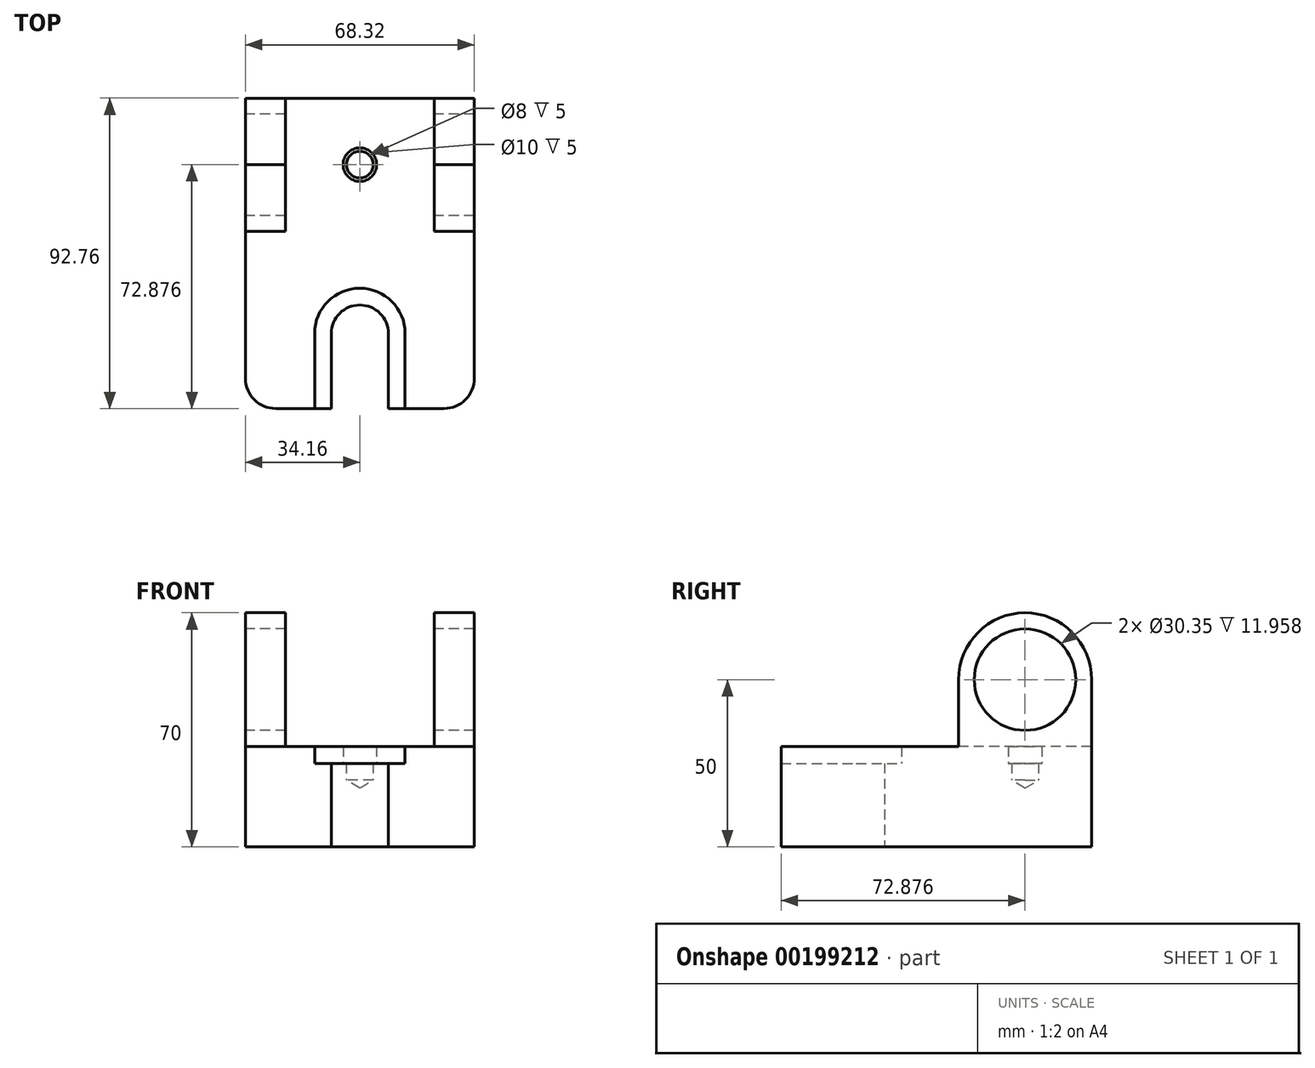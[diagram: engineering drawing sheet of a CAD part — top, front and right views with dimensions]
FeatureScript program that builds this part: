
annotation { "Feature Type Name" : "Feature", "Feature Type Description" : "" }
export const myFeature = defineFeature(function(context is Context, id is Id, definition is map)
    precondition{}
    {
        {
            var Q0;
            Q0=qCreatedBy(makeId("Top.planeOp"),FACE);
            var sketch = newSketch(context, id + "F0", { "sketchPlane" : qUnion([Q0])});
            skLineSegment(sketch, "E0.bottom", {"start": v(34.16, 46.38) * mm, "end": v(-34.16, 46.38) * mm});
            skLineSegment(sketch, "E0.top", {"start": v(34.16, -46.38) * mm, "end": v(13.5, -46.38) * mm});
            skLineSegment(sketch, "E0.left", {"start": v(34.16, 46.38) * mm, "end": v(34.16, -46.38) * mm});
            skLineSegment(sketch, "E0.right", {"start": v(-34.16, 46.38) * mm, "end": v(-34.16, -46.38) * mm});
            skPoint(sketch, "E0.middle", {"position": v(0, 0) * mm});
            skLineSegment(sketch, "E1", {"start": v(-13.5, -46.38) * mm, "end": v(-13.5, -23.93) * mm});
            skLineSegment(sketch, "E2", {"start": v(0, 46.38) * mm, "end": v(0, -46.38) * mm, "construction": true});
            skLineSegment(sketch, "E3.MirrorCS", {"start": v(13.5, -46.38) * mm, "end": v(13.5, -23.93) * mm});
            skArc(sketch, "E4", {"start": v(13.5, -23.93) * mm, "mid": v(0, -10.43) * mm, "end": v(-13.5, -23.93) * mm});
            skLineSegment(sketch, "E5.trimOffspring", {"start": v(-13.5, -46.38) * mm, "end": v(-34.16, -46.38) * mm});
            skLineSegment(sketch, "E6.0", {"start": v(8.5, -46.38) * mm, "end": v(8.5, -23.93) * mm});
            skArc(sketch, "E6.1", {"start": v(8.5, -23.93) * mm, "mid": v(0, -15.43) * mm, "end": v(-8.5, -23.93) * mm});
            skLineSegment(sketch, "E6.2", {"start": v(-8.5, -46.38) * mm, "end": v(-8.5, -23.93) * mm});
            skLineSegment(sketch, "E7", {"start": v(-13.5, -46.38) * mm, "end": v(-8.5, -46.38) * mm});
            skLineSegment(sketch, "E8", {"start": v(8.5, -46.38) * mm, "end": v(13.5, -46.38) * mm});
            skSolve(sketch);
        }
        {
            var Q0;
            Q0=makeQuery(id+"F0.imprint","IMPRINT",FACE,{"disambiguationData":[TD([[makeQuery(id+"F0.imprint","IMPRINT",EDGE,{"derivedFrom":sQuery(id+"F0.wireOp",EDGE,"E1")}),-1.0]])]});
            extrude(context, id + "F1", {"entities" : qUnion([Q0]), "depth" : 25 * mm});
        }
        {
            var Q0;
            Q0=makeQuery(id+"F0.imprint","IMPRINT",FACE,{"disambiguationData":[TD([[makeQuery(id+"F0.imprint","IMPRINT",EDGE,{"derivedFrom":sQuery(id+"F0.wireOp",EDGE,"E0.bottom")}),1.0]])]});
            extrude(context, id + "F2", {"entities" : qUnion([Q0]), "operationType" : NewBodyOperationType.ADD, "depth" : 30 * mm});
        }
        {
            var Q0;
            Q0=makeQuery(id+"F2.opExtrude","CAP_FACE",FACE,{"disambiguationData":[OSD([sQuery(id+"F0.wireOp",EDGE,"E0.bottom"),sQuery(id+"F0.wireOp",EDGE,"E0.top"),sQuery(id+"F0.wireOp",EDGE,"E0.left"),sQuery(id+"F0.wireOp",EDGE,"E0.right"),sQuery(id+"F0.wireOp",EDGE,"E1"),sQuery(id+"F0.wireOp",EDGE,"E3.MirrorCS"),sQuery(id+"F0.wireOp",EDGE,"E4"),sQuery(id+"F0.wireOp",EDGE,"E5.trimOffspring")])],"isStart":false});
            var sketch = newSketch(context, id + "F3", { "sketchPlane" : qUnion([Q0])});
            skLineSegment(sketch, "E9.bottom", {"start": v(34.16, 46.38) * mm, "end": v(22.2, 46.38) * mm});
            skLineSegment(sketch, "E9.top", {"start": v(34.16, 6.62) * mm, "end": v(22.2, 6.62) * mm});
            skLineSegment(sketch, "E9.left", {"start": v(34.16, 46.38) * mm, "end": v(34.16, 6.62) * mm});
            skLineSegment(sketch, "E9.right", {"start": v(22.2, 46.38) * mm, "end": v(22.2, 6.62) * mm});
            skLineSegment(sketch, "E10.MirrorCS", {"start": v(-22.2, 46.38) * mm, "end": v(-22.2, 6.62) * mm});
            skLineSegment(sketch, "E11.MirrorCS", {"start": v(-34.16, 6.62) * mm, "end": v(-22.2, 6.62) * mm});
            skLineSegment(sketch, "E12.MirrorCS", {"start": v(-34.16, 46.38) * mm, "end": v(-34.16, 6.62) * mm});
            skLineSegment(sketch, "E13.MirrorCS", {"start": v(-34.16, 46.38) * mm, "end": v(-22.2, 46.38) * mm});
            skSolve(sketch);
        }
        {
            var Q0;
            Q0=makeQuery(id+"F3.imprint","IMPRINT",FACE,{"disambiguationData":[TD([[makeQuery(id+"F3.imprint","IMPRINT",EDGE,{"derivedFrom":sQuery(id+"F3.wireOp",EDGE,"E9.bottom")}),1.0]])]});
            var Q1;
            Q1=makeQuery(id+"F3.imprint","IMPRINT",FACE,{"disambiguationData":[TD([[makeQuery(id+"F3.imprint","IMPRINT",EDGE,{"derivedFrom":sQuery(id+"F3.wireOp",EDGE,"E10.MirrorCS")}),-1.0]])]});
            extrude(context, id + "F4", {"entities" : qUnion([Q0, Q1]), "operationType" : NewBodyOperationType.ADD, "depth" : 40 * mm});
        }
        {
            var Q0;
            Q0=makeQuery(id+"F4.boolean.opBoolean","MERGE",FACE,{"derivedFrom":[makeQuery(id+"F2.opExtrude","SWEPT_FACE",FACE,{"disambiguationData":[OSD([sQuery(id+"F0.wireOp",EDGE,"E0.right")])]}),makeQuery(id+"F4.opExtrude","SWEPT_FACE",FACE,{"disambiguationData":[OSD([sQuery(id+"F3.wireOp",EDGE,"E12.MirrorCS")])]})]});
            var sketch = newSketch(context, id + "F5", { "sketchPlane" : qUnion([Q0])});
            skPoint(sketch, "E14", {"position": v(-26.5, 50) * mm});
            skPoint(sketch, "E14.positionSnap0", {"position": v(-6.62, 50) * mm});
            skPoint(sketch, "E14.positionSnap1", {"position": v(-26.5, 70) * mm});
            skCircle(sketch, "E15", {"center": v(-26.5, 50) * mm, "radius": 15.17 * mm});
            skSolve(sketch);
        }
        {
            var Q0;
            Q0=makeQuery(id+"F5.imprint","IMPRINT",FACE,{"disambiguationData":[TD([[makeQuery(id+"F5.imprint","IMPRINT",EDGE,{"derivedFrom":sQuery(id+"F5.wireOp",EDGE,"E15")}),1.0]])]});
            extrude(context, id + "F6", {"entities" : qUnion([Q0]), "operationType" : NewBodyOperationType.REMOVE, "endBound" : BoundingType.THROUGH_ALL, "oppositeDirection" : true, "depth" : 25 * mm});
        }
        {
            var Q0;
            Q0=makeQuery(id+"F4.opExtrude","CAP_EDGE",EDGE,{"disambiguationData":[OSD([sQuery(id+"F3.wireOp",EDGE,"E11.MirrorCS")])],"isStart":false});
            var Q1;
            Q1=makeQuery(id+"F4.opExtrude","CAP_EDGE",EDGE,{"disambiguationData":[OSD([sQuery(id+"F3.wireOp",EDGE,"E9.top")])],"isStart":false});
            var Q2;
            Q2=makeQuery(id+"F4.opExtrude","CAP_EDGE",EDGE,{"disambiguationData":[OSD([sQuery(id+"F3.wireOp",EDGE,"E9.bottom")])],"isStart":false});
            var Q3;
            Q3=makeQuery(id+"F4.opExtrude","CAP_EDGE",EDGE,{"disambiguationData":[OSD([sQuery(id+"F3.wireOp",EDGE,"E13.MirrorCS")])],"isStart":false});
            fillet(context, id + "F7", {"entities" : qUnion([Q0, Q1, Q2, Q3]), "radius" : 20 * mm, "tangentPropagation" : true, "allowEdgeOverflow" : false});
        }
        {
            var Q0;
            Q0=makeQuery(id+"F2.opExtrude","SWEPT_EDGE",EDGE,{"disambiguationData":[OSD([sQuery(id+"F0.wireOp",EDGE,"E0.top"),sQuery(id+"F0.wireOp",EDGE,"E0.left")])]});
            var Q1;
            Q1=makeQuery(id+"F2.opExtrude","SWEPT_EDGE",EDGE,{"disambiguationData":[OSD([sQuery(id+"F0.wireOp",EDGE,"E0.right"),sQuery(id+"F0.wireOp",EDGE,"E5.trimOffspring")])]});
            fillet(context, id + "F8", {"entities" : qUnion([Q0, Q1]), "radius" : 9 * mm, "tangentPropagation" : true, "allowEdgeOverflow" : false});
        }
        {
            var Q0;
            Q0=makeQuery(id+"F2.opExtrude","CAP_FACE",FACE,{"disambiguationData":[OSD([sQuery(id+"F0.wireOp",EDGE,"E0.bottom"),sQuery(id+"F0.wireOp",EDGE,"E0.top"),sQuery(id+"F0.wireOp",EDGE,"E0.left"),sQuery(id+"F0.wireOp",EDGE,"E0.right"),sQuery(id+"F0.wireOp",EDGE,"E1"),sQuery(id+"F0.wireOp",EDGE,"E3.MirrorCS"),sQuery(id+"F0.wireOp",EDGE,"E4"),sQuery(id+"F0.wireOp",EDGE,"E5.trimOffspring")])],"isStart":false});
            var sketch = newSketch(context, id + "F9", { "sketchPlane" : qUnion([Q0])});
            skLineSegment(sketch, "E16", {"start": v(0, -10.43) * mm, "end": v(0, 46.38) * mm, "construction": true});
            skPoint(sketch, "E17", {"position": v(0, 26.5) * mm});
            skLineSegment(sketch, "E18", {"start": v(-22.2, 26.5) * mm, "end": v(22.2, 26.5) * mm, "construction": true});
            skSolve(sketch);
        }
        {
            var Q0;
            Q0=sQuery(id+"F9.wireOp",VERTEX,"E17");
            var Q1;
            Q1=makeQuery(id+"F1.opExtrude","SWEPT_BODY",BODY,{"disambiguationData":[OSD([sQuery(id+"F0.wireOp",EDGE,"E1"),sQuery(id+"F0.wireOp",EDGE,"E3.MirrorCS"),sQuery(id+"F0.wireOp",EDGE,"E4"),sQuery(id+"F0.wireOp",EDGE,"E6.0"),sQuery(id+"F0.wireOp",EDGE,"E6.1"),sQuery(id+"F0.wireOp",EDGE,"E6.2"),sQuery(id+"F0.wireOp",EDGE,"E7"),sQuery(id+"F0.wireOp",EDGE,"E8")])]});
            hole(context, id + "F10", {"style" : HoleStyle.C_BORE, "endStyle" : HoleEndStyle.BLIND, "holeDiameter" : 8 * mm, "cBoreDiameter" : 10 * mm, "cBoreDepth" : 5 * mm, "holeDepth" : 10 * mm, "locations" : qUnion([Q0]), "scope" : qUnion([Q1]), "startStyle" : HoleStartStyle.PART});
        }
    });
